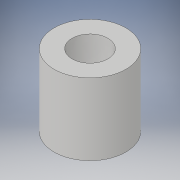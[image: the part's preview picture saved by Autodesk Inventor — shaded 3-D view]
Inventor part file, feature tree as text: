
AUTODESK INVENTOR PART (.ipt)
format: ipt  version: 2017 (Build 210142000, 142)  size: 96,768 bytes
history: native  units: in
note: dims shown in document units (in); Inventor stores cm internally (conversion verified against a paired STEP export)
features: extrude x1, sketch x1
ambient origin geometry x8: Origin, YZ Plane, XZ Plane, XY Plane, X Axis, Y Axis, Z Axis, Center Point
bodies: Solid1 (feature_tree)
feature tree (2):
  extrude  "Extrusion1"  Depth=0.5in
  sketch  "Sketch1"  dims[d0=0.25in d1=0.5in d2=0.5in d3=0.0in]
